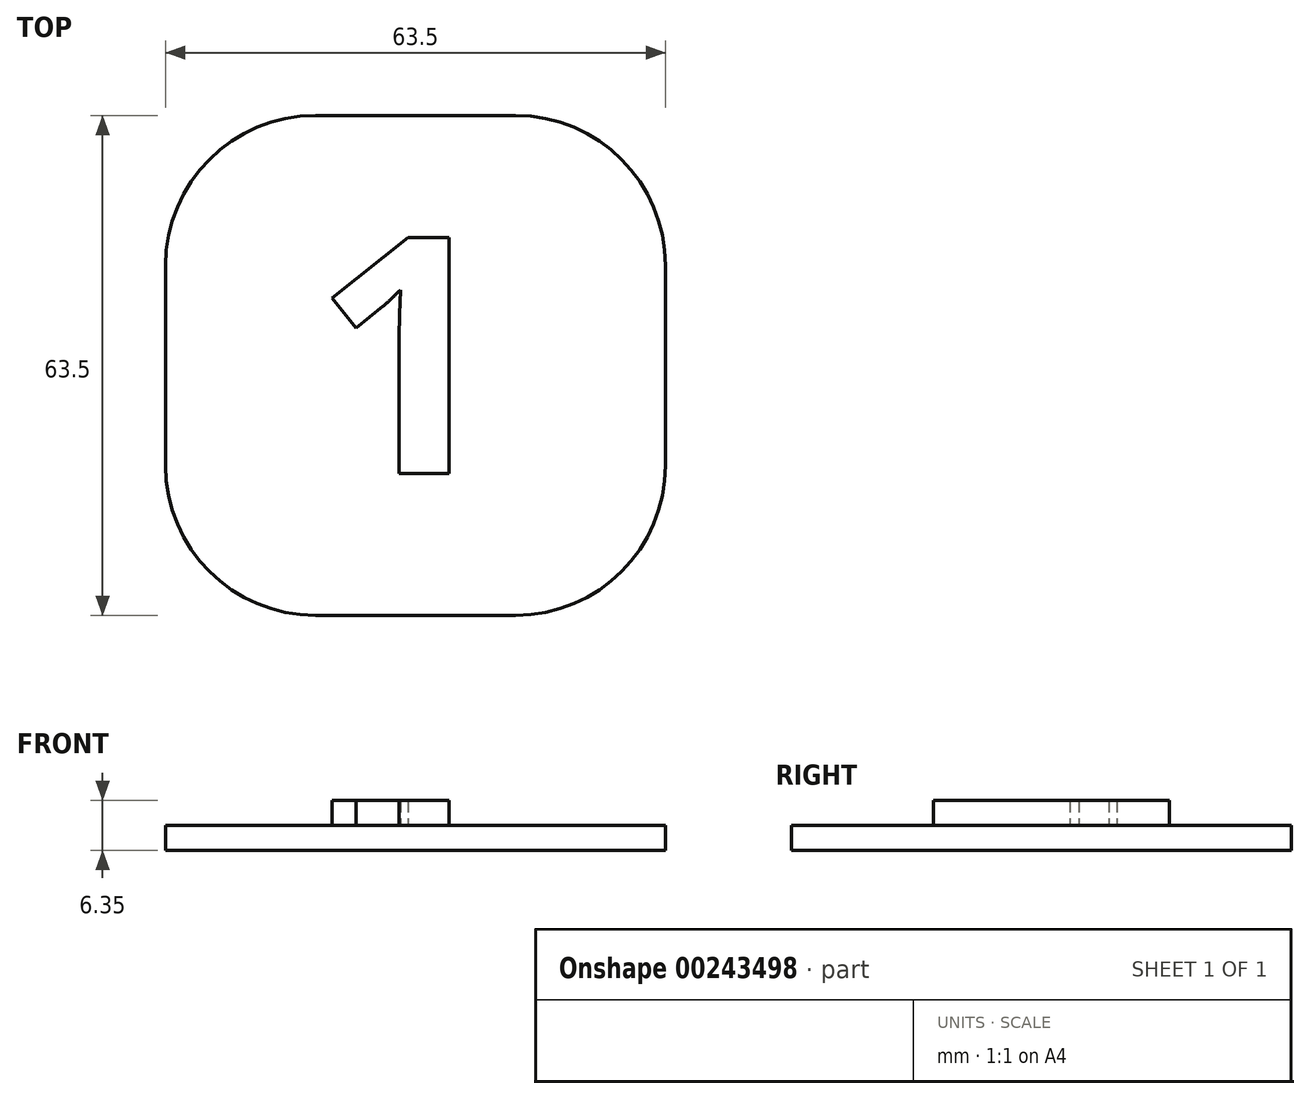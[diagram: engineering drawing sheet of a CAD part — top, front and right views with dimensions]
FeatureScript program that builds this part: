
annotation { "Feature Type Name" : "Feature", "Feature Type Description" : "" }
export const myFeature = defineFeature(function(context is Context, id is Id, definition is map)
    precondition{}
    {
        {
            var Q0;
            Q0=qCreatedBy(makeId("Top.planeOp"),FACE);
            var sketch = newSketch(context, id + "F0", { "sketchPlane" : qUnion([Q0])});
            skLineSegment(sketch, "E0.bottom", {"start": v(0.4, 32.05) * mm, "end": v(25.8, 32.05) * mm});
            skLineSegment(sketch, "E0.top", {"start": v(0.4, -31.45) * mm, "end": v(25.8, -31.45) * mm});
            skLineSegment(sketch, "E0.left", {"start": v(-18.64, 13) * mm, "end": v(-18.64, -12.4) * mm});
            skLineSegment(sketch, "E0.right", {"start": v(44.86, 13) * mm, "end": v(44.86, -12.4) * mm});
            skPoint(sketch, "E1.visualSharp", {"position": v(-18.64, 32.05) * mm});
            skArc(sketch, "E1.filletArc", {"start": v(0.4, 32.05) * mm, "mid": v(-13.06, 26.47) * mm, "end": v(-18.64, 13) * mm});
            skPoint(sketch, "E2.visualSharp", {"position": v(44.86, 32.05) * mm});
            skArc(sketch, "E2.filletArc", {"start": v(44.86, 13) * mm, "mid": v(39.28, 26.47) * mm, "end": v(25.8, 32.05) * mm});
            skPoint(sketch, "E3.visualSharp", {"position": v(-18.64, -31.45) * mm});
            skArc(sketch, "E3.filletArc", {"start": v(-18.64, -12.4) * mm, "mid": v(-13.06, -25.87) * mm, "end": v(0.4, -31.45) * mm});
            skPoint(sketch, "E4.visualSharp", {"position": v(44.86, -31.45) * mm});
            skArc(sketch, "E4.filletArc", {"start": v(25.8, -31.45) * mm, "mid": v(39.28, -25.87) * mm, "end": v(44.86, -12.4) * mm});
            skSolve(sketch);
        }
        {
            var Q0;
            Q0 = qSketchRegion(id + "F0", true);
            extrude(context, id + "F1", {"entities" : qUnion([Q0]), "depth" : 3.17 * mm});
        }
        {
            var Q0;
            Q0=makeQuery(id+"F1.opExtrude","CAP_FACE",FACE,{"disambiguationData":[OSD([sQuery(id+"F0.wireOp",EDGE,"E0.bottom"),sQuery(id+"F0.wireOp",EDGE,"E0.top"),sQuery(id+"F0.wireOp",EDGE,"E0.left"),sQuery(id+"F0.wireOp",EDGE,"E0.right"),sQuery(id+"F0.wireOp",EDGE,"E1.filletArc"),sQuery(id+"F0.wireOp",EDGE,"E2.filletArc"),sQuery(id+"F0.wireOp",EDGE,"E3.filletArc"),sQuery(id+"F0.wireOp",EDGE,"E4.filletArc")])],"isStart":false});
            var sketch = newSketch(context, id + "F2", { "sketchPlane" : qUnion([Q0])});
            skText(sketch, "E5", { "text": "1", "fontName": "OpenSans-Bold.ttf"});
            const initialGuessF2  = {"E5": [0, -0.01342, 1, 0, 0.03024]};
            skSetInitialGuess(sketch, initialGuessF2);
            skSolve(sketch);
        }
        {
            var Q0;
            Q0 = qSketchRegion(id + "F2", true);
            extrude(context, id + "F3", {"entities" : qUnion([Q0]), "operationType" : NewBodyOperationType.ADD, "depth" : 3.17 * mm});
        }
    });
